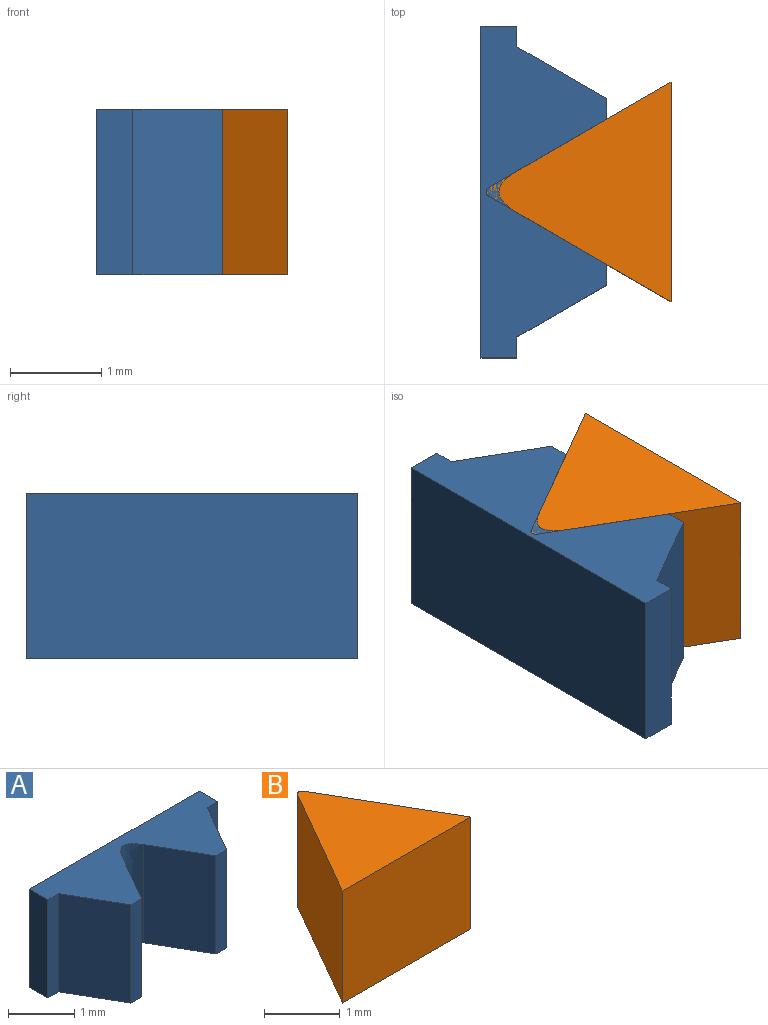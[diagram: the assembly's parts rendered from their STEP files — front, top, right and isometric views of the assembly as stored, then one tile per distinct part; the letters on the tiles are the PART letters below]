
ASSEMBLY  parts=2 mates=3
PART A: 14 faces, bbox 3.6x1.4x1.8 mm
  f0: plane 1.81x0.23mm, normal (0,-1,0), area 0.4mm2, adj f1,f11,f12,f13
  f1: plane 1.81x0.98mm, normal (0.87,-0.5,0), area 2.1mm2, adj f0,f2,f12,f13
  f2: extruded ~1.81x0.45mm, area 1.1mm2, adj f1,f3,f12,f13
  f3: plane 1.81x0.98mm, normal (-0.87,-0.5,0), area 2.1mm2, adj f2,f4,f12,f13
  f4: plane 1.81x0.23mm, normal (0,-1,0), area 0.4mm2, adj f3,f5,f12,f13
  f5: plane 1.81x0.98mm, normal (0.87,-0.5,0), area 2.1mm2, adj f4,f6,f12,f13
  f6: plane 1.81x0.23mm, normal (0,-1,0), area 0.4mm2, adj f5,f7,f12,f13
  f7: plane 1.81x0.39mm, normal (1,0,0), area 0.7mm2, adj f6,f8,f12,f13
  f8: plane 3.63x1.81mm, normal (0,1,0), area 6.6mm2, adj f7,f9,f12,f13
  f9: plane 1.81x0.39mm, normal (-1,0,0), area 0.7mm2, adj f8,f10,f12,f13
  f10: plane 1.81x0.23mm, normal (0,-1,0), area 0.4mm2, adj f9,f11,f12,f13
  f11: plane 1.81x0.98mm, normal (-0.87,-0.5,0), area 2.1mm2, adj f0,f10,f12,f13
  f12: plane 3.63x1.38mm, normal (0,0,1), area 2.9mm2, adj f0,f1,f2,f3,f4,f5,f6,f7
  f13: plane 3.63x1.38mm, normal (0,0,-1), area 2.9mm2, adj f0,f1,f2,f3,f4,f5,f6,f7
PART B: 6 faces, bbox 2.4x2x1.8 mm
  f0: cylinder r=0.06mm len=1.81mm, axis (0,0,-1), area 0.2mm2, adj f1,f3,f4,f5
  f1: plane 1.99x1.81mm, normal (-0.87,0.5,0), area 4.2mm2, adj f0,f2,f4,f5
  f2: plane 2.4x1.81mm, normal (0,-1,0), area 4.4mm2, adj f1,f3,f4,f5
  f3: plane 1.99x1.81mm, normal (0.87,0.5,0), area 4.2mm2, adj f0,f2,f4,f5
  f4: plane 2.4x2.02mm, normal (0,0,1), area 2.5mm2, adj f0,f1,f2,f3
  f5: plane 2.4x2.02mm, normal (0,0,-1), area 2.5mm2, adj f0,f1,f2,f3
PLACE A rot(axis=(0,0,1),90deg) t=(0,0,0)mm
PLACE B rot(axis=(0,0,1),90deg) t=(0,0,0)mm
MATE planar A.f1 <-> B.f1  axis (0.5,0.87,0) through (0.88,-0.51,0.91)mm
MATE planar B.f4 <-> A.f12  axis (0,0,1) through (1.39,0,1.81)mm
MATE planar B.f3 <-> A.f3  axis (-0.5,0.87,0) through (1.08,0.63,0.91)mm
